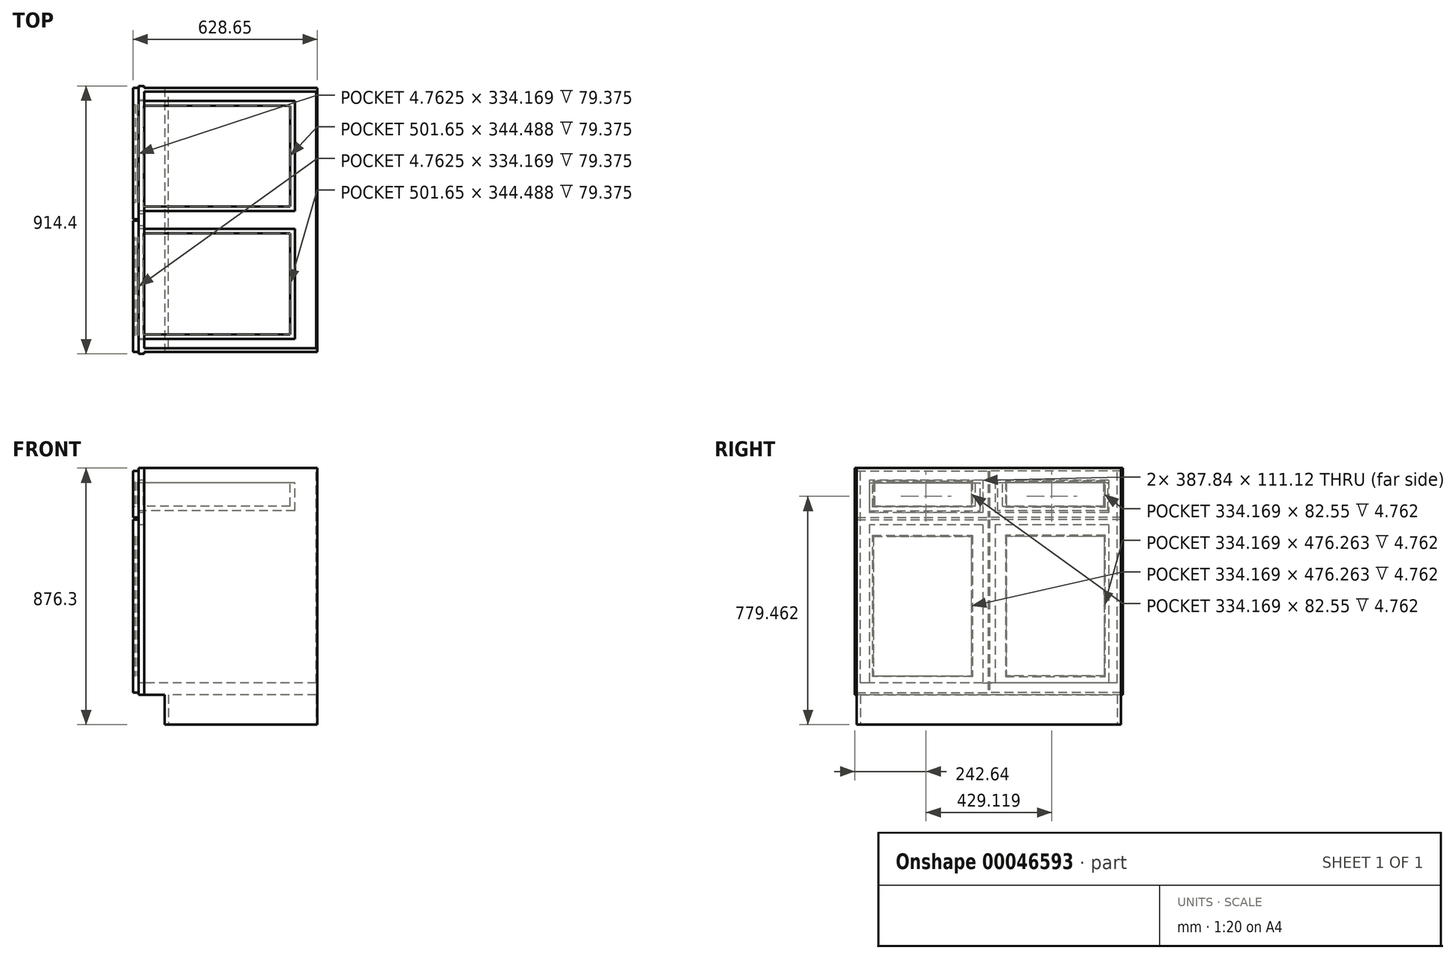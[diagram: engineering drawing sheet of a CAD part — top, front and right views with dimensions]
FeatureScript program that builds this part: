
annotation { "Feature Type Name" : "Feature", "Feature Type Description" : "" }
export const myFeature = defineFeature(function(context is Context, id is Id, definition is map)
    precondition{}
    {
        {
            var Q0;
            Q0=qCreatedBy(makeId("Front.planeOp"),FACE);
            var sketch = newSketch(context, id + "F0", { "sketchPlane" : qUnion([Q0])});
            skLineSegment(sketch, "E0.bottom", {"start": v(-304.8, -438.15) * mm, "end": v(304.8, -438.15) * mm});
            skLineSegment(sketch, "E0.top", {"start": v(-304.8, 438.15) * mm, "end": v(304.8, 438.15) * mm});
            skLineSegment(sketch, "E0.left", {"start": v(-304.8, -438.15) * mm, "end": v(-304.8, 438.15) * mm});
            skLineSegment(sketch, "E0.right", {"start": v(304.8, -438.15) * mm, "end": v(304.8, 438.15) * mm});
            skLineSegment(sketch, "E1", {"start": v(-304.8, -438.15) * mm, "end": v(304.8, 438.15) * mm, "construction": true});
            skSolve(sketch);
        }
        {
            var Q0;
            Q0=qSketchRegion(id+"F0",true);
            extrude(context, id + "F1", {"entities" : qUnion([Q0]), "oppositeDirection" : true, "depth" : 914.4 * mm});
        }
        {
            var Q0;
            Q0=makeQuery(id+"F1.opExtrude","CAP_FACE",FACE,{"disambiguationData":[OSD([sQuery(id+"F0.wireOp",EDGE,"E0.bottom"),sQuery(id+"F0.wireOp",EDGE,"E0.top"),sQuery(id+"F0.wireOp",EDGE,"E0.left"),sQuery(id+"F0.wireOp",EDGE,"E0.right")])],"isStart":true});
            var sketch = newSketch(context, id + "F2", { "sketchPlane" : qUnion([Q0])});
            skLineSegment(sketch, "E2.bottom", {"start": v(-304.8, -438.15) * mm, "end": v(-215.9, -438.15) * mm});
            skLineSegment(sketch, "E2.top", {"start": v(-304.8, -336.55) * mm, "end": v(-215.9, -336.55) * mm});
            skLineSegment(sketch, "E2.left", {"start": v(-304.8, -438.15) * mm, "end": v(-304.8, -336.55) * mm});
            skLineSegment(sketch, "E2.right", {"start": v(-215.9, -438.15) * mm, "end": v(-215.9, -336.55) * mm});
            skSolve(sketch);
        }
        {
            var Q0;
            Q0=qSketchRegion(id+"F2",true);
            extrude(context, id + "F3", {"entities" : qUnion([Q0]), "operationType" : NewBodyOperationType.REMOVE, "endBound" : BoundingType.THROUGH_ALL, "oppositeDirection" : true, "depth" : 25.4 * mm});
        }
        {
            var Q0;
            Q0=makeQuery(id+"F1.opExtrude","SWEPT_FACE",FACE,{"disambiguationData":[OSD([sQuery(id+"F0.wireOp",EDGE,"E0.left")])]});
            var sketch = newSketch(context, id + "F4", { "sketchPlane" : qUnion([Q0])});
            skLineSegment(sketch, "E3.bottom", {"start": v(-865.68, 396.88) * mm, "end": v(-48.72, 396.88) * mm});
            skLineSegment(sketch, "E3.top", {"start": v(-865.68, -295.28) * mm, "end": v(-48.72, -295.28) * mm});
            skLineSegment(sketch, "E3.left", {"start": v(-865.68, 396.88) * mm, "end": v(-865.68, -295.28) * mm});
            skLineSegment(sketch, "E3.right", {"start": v(-48.72, 396.88) * mm, "end": v(-48.72, -295.28) * mm});
            skLineSegment(sketch, "E4", {"start": v(-914.4, 438.15) * mm, "end": v(0, -336.55) * mm, "construction": true});
            skSolve(sketch);
        }
        {
            var Q0;
            Q0=qSketchRegion(id+"F4",true);
            extrude(context, id + "F5", {"entities" : qUnion([Q0]), "operationType" : NewBodyOperationType.REMOVE, "oppositeDirection" : true, "depth" : 19.05 * mm});
        }
        {
            var Q0;
            Q0=makeQuery(id+"F1.opExtrude","SWEPT_FACE",FACE,{"disambiguationData":[OSD([sQuery(id+"F0.wireOp",EDGE,"E0.top")])]});
            var sketch = newSketch(context, id + "F6", { "sketchPlane" : qUnion([Q0])});
            skLineSegment(sketch, "E5.bottom", {"start": v(304.8, 914.4) * mm, "end": v(-285.75, 914.4) * mm});
            skLineSegment(sketch, "E5.top", {"start": v(304.8, 908.05) * mm, "end": v(-285.75, 908.05) * mm});
            skLineSegment(sketch, "E5.left", {"start": v(304.8, 914.4) * mm, "end": v(304.8, 908.05) * mm});
            skLineSegment(sketch, "E5.right", {"start": v(-285.75, 914.4) * mm, "end": v(-285.75, 908.05) * mm});
            skLineSegment(sketch, "E6.bottom", {"start": v(304.8, 0) * mm, "end": v(-285.75, 0) * mm});
            skLineSegment(sketch, "E6.top", {"start": v(304.8, 6.35) * mm, "end": v(-285.75, 6.35) * mm});
            skLineSegment(sketch, "E6.left", {"start": v(304.8, 0) * mm, "end": v(304.8, 6.35) * mm});
            skLineSegment(sketch, "E6.right", {"start": v(-285.75, 0) * mm, "end": v(-285.75, 6.35) * mm});
            skSolve(sketch);
        }
        {
            var Q0;
            Q0=qSketchRegion(id+"F6",true);
            extrude(context, id + "F7", {"entities" : qUnion([Q0]), "operationType" : NewBodyOperationType.REMOVE, "endBound" : BoundingType.THROUGH_ALL, "oppositeDirection" : true, "depth" : 25.4 * mm});
        }
        {
            var Q0;
            Q0=makeQuery(id+"F1.opExtrude","SWEPT_FACE",FACE,{"disambiguationData":[OSD([sQuery(id+"F0.wireOp",EDGE,"E0.top")])]});
            var sketch = newSketch(context, id + "F8", { "sketchPlane" : qUnion([Q0])});
            skLineSegment(sketch, "E7.bottom", {"start": v(301.62, 895.35) * mm, "end": v(-285.75, 895.35) * mm});
            skLineSegment(sketch, "E7.top", {"start": v(301.63, 19.05) * mm, "end": v(-285.75, 19.05) * mm});
            skLineSegment(sketch, "E7.left", {"start": v(301.62, 895.35) * mm, "end": v(301.63, 19.05) * mm});
            skLineSegment(sketch, "E7.right", {"start": v(-285.75, 895.35) * mm, "end": v(-285.75, 19.05) * mm});
            skSolve(sketch);
        }
        {
            var Q0;
            Q0=qSketchRegion(id+"F8",true);
            var Q1;
            Q1=makeQuery(id+"F5.boolean.opBoolean","COPY",FACE,{"derivedFrom":makeQuery(id+"F5.opExtrude","SWEPT_FACE",FACE,{"disambiguationData":[OSD([sQuery(id+"F4.wireOp",EDGE,"E3.top")])]})});
            extrude(context, id + "F9", {"entities" : qUnion([Q0]), "operationType" : NewBodyOperationType.REMOVE, "endBound" : BoundingType.UP_TO_SURFACE, "oppositeDirection" : true, "endBoundEntityFace" : qUnion([Q1]), "depth" : 25.4 * mm});
        }
        {
            var Q0;
            Q0=makeQuery(id+"F1.opExtrude","SWEPT_FACE",FACE,{"disambiguationData":[OSD([sQuery(id+"F0.wireOp",EDGE,"E0.left")])]});
            var sketch = newSketch(context, id + "F10", { "sketchPlane" : qUnion([Q0])});
            skLineSegment(sketch, "E8.bottom", {"start": v(-865.68, 285.75) * mm, "end": v(-48.72, 285.75) * mm});
            skLineSegment(sketch, "E8.top", {"start": v(-865.68, 244.47) * mm, "end": v(-48.72, 244.47) * mm});
            skLineSegment(sketch, "E8.left", {"start": v(-865.68, 285.75) * mm, "end": v(-865.68, 244.47) * mm});
            skLineSegment(sketch, "E8.right", {"start": v(-48.72, 285.75) * mm, "end": v(-48.72, 244.47) * mm});
            skLineSegment(sketch, "E9", {"start": v(-457.2, 396.88) * mm, "end": v(-457.2, -295.28) * mm, "construction": true});
            skLineSegment(sketch, "E10.bottom", {"start": v(-477.84, 396.88) * mm, "end": v(-436.56, 396.88) * mm});
            skLineSegment(sketch, "E10.top", {"start": v(-477.84, -295.28) * mm, "end": v(-436.56, -295.28) * mm});
            skLineSegment(sketch, "E10.left", {"start": v(-477.84, 396.87) * mm, "end": v(-477.84, -295.28) * mm});
            skLineSegment(sketch, "E10.right", {"start": v(-436.56, 396.87) * mm, "end": v(-436.56, -295.28) * mm});
            skSolve(sketch);
        }
        {
            var Q0;
            Q0=qSketchRegion(id+"F10",true);
            var Q1;
            Q1=makeQuery(id+"F9.boolean.opBoolean","COPY",FACE,{"derivedFrom":makeQuery(id+"F9.opExtrude","SWEPT_FACE",FACE,{"disambiguationData":[OSD([sQuery(id+"F8.wireOp",EDGE,"E7.right")])]})});
            extrude(context, id + "F11", {"entities" : qUnion([Q0]), "operationType" : NewBodyOperationType.ADD, "endBound" : BoundingType.UP_TO_SURFACE, "oppositeDirection" : true, "endBoundEntityFace" : qUnion([Q1]), "depth" : 25.4 * mm});
        }
        {
            var Q0;
            Q0=makeQuery(id+"F11.boolean.opBoolean","MERGE",FACE,{"derivedFrom":[makeQuery(id+"F1.opExtrude","SWEPT_FACE",FACE,{"disambiguationData":[OSD([sQuery(id+"F0.wireOp",EDGE,"E0.left")])]}),makeQuery(id+"F11.opExtrude","CAP_FACE",FACE,{"disambiguationData":[OSD([sQuery(id+"F10.wireOp",EDGE,"E8.bottom"),sQuery(id+"F10.wireOp",EDGE,"E8.top"),sQuery(id+"F10.wireOp",EDGE,"E8.left"),sQuery(id+"F10.wireOp",EDGE,"E8.right"),sQuery(id+"F10.wireOp",EDGE,"E10.bottom"),sQuery(id+"F10.wireOp",EDGE,"E10.top"),sQuery(id+"F10.wireOp",EDGE,"E10.left"),sQuery(id+"F10.wireOp",EDGE,"E10.right")])],"isStart":true})]});
            var sketch = newSketch(context, id + "F12", { "sketchPlane" : qUnion([Q0])});
            skLineSegment(sketch, "E11.bottom", {"start": v(-908.05, 261.95) * mm, "end": v(-459.58, 261.95) * mm});
            skLineSegment(sketch, "E11.top", {"start": v(-908.05, -328.61) * mm, "end": v(-459.58, -328.61) * mm});
            skLineSegment(sketch, "E11.left", {"start": v(-908.05, 261.95) * mm, "end": v(-908.05, -328.61) * mm});
            skLineSegment(sketch, "E11.right", {"start": v(-459.58, 261.95) * mm, "end": v(-459.58, -328.61) * mm});
            skLineSegment(sketch, "E12.bottom", {"start": v(-850.9, 204.8) * mm, "end": v(-516.73, 204.8) * mm});
            skLineSegment(sketch, "E12.top", {"start": v(-850.9, -271.46) * mm, "end": v(-516.73, -271.46) * mm});
            skLineSegment(sketch, "E12.left", {"start": v(-850.9, 204.8) * mm, "end": v(-850.9, -271.46) * mm});
            skLineSegment(sketch, "E12.right", {"start": v(-516.73, 204.8) * mm, "end": v(-516.73, -271.46) * mm});
            skSolve(sketch);
        }
        {
            var Q0;
            Q0=qSketchRegion(id+"F12",true);
            extrude(context, id + "F13", {"entities" : qUnion([Q0]), "depth" : 19.05 * mm});
        }
        {
            var Q0;
            Q0=makeQuery(id+"F13.opExtrude","SWEPT_FACE",FACE,{"disambiguationData":[OSD([sQuery(id+"F12.wireOp",EDGE,"E12.top")])]});
            var sketch = newSketch(context, id + "F14", { "sketchPlane" : qUnion([Q0])});
            skLineSegment(sketch, "E13.bottom", {"start": v(-315.91, 850.9) * mm, "end": v(-309.56, 850.9) * mm});
            skLineSegment(sketch, "E13.top", {"start": v(-315.91, 516.73) * mm, "end": v(-309.56, 516.73) * mm});
            skLineSegment(sketch, "E13.left", {"start": v(-315.91, 850.9) * mm, "end": v(-315.91, 516.73) * mm});
            skLineSegment(sketch, "E13.right", {"start": v(-309.56, 850.9) * mm, "end": v(-309.56, 516.73) * mm});
            skSolve(sketch);
        }
        {
            var Q0;
            Q0=qSketchRegion(id+"F14",true);
            extrude(context, id + "F15", {"entities" : qUnion([Q0]), "operationType" : NewBodyOperationType.ADD, "endBound" : BoundingType.UP_TO_NEXT, "depth" : 25.4 * mm});
        }
        {
            var Q0;
            Q0=makeQuery(id+"F13.opExtrude","CAP_EDGE",EDGE,{"disambiguationData":[OSD([sQuery(id+"F12.wireOp",EDGE,"E12.left")])],"isStart":false});
            var Q1;
            Q1=makeQuery(id+"F13.opExtrude","CAP_EDGE",EDGE,{"disambiguationData":[OSD([sQuery(id+"F12.wireOp",EDGE,"E12.top")])],"isStart":false});
            var Q2;
            Q2=makeQuery(id+"F13.opExtrude","CAP_EDGE",EDGE,{"disambiguationData":[OSD([sQuery(id+"F12.wireOp",EDGE,"E12.right")])],"isStart":false});
            var Q3;
            Q3=makeQuery(id+"F13.opExtrude","CAP_EDGE",EDGE,{"disambiguationData":[OSD([sQuery(id+"F12.wireOp",EDGE,"E12.bottom")])],"isStart":false});
            chamfer(context, id + "F16", {"entities" : qUnion([Q0, Q1, Q2, Q3]), "width" : 3.17 * mm, "tangentPropagation" : true});
        }
        {
            var Q0;
            Q0=makeQuery(id+"F11.boolean.opBoolean","MERGE",FACE,{"derivedFrom":[makeQuery(id+"F1.opExtrude","SWEPT_FACE",FACE,{"disambiguationData":[OSD([sQuery(id+"F0.wireOp",EDGE,"E0.left")])]}),makeQuery(id+"F11.opExtrude","CAP_FACE",FACE,{"disambiguationData":[OSD([sQuery(id+"F10.wireOp",EDGE,"E8.bottom"),sQuery(id+"F10.wireOp",EDGE,"E8.top"),sQuery(id+"F10.wireOp",EDGE,"E8.left"),sQuery(id+"F10.wireOp",EDGE,"E8.right"),sQuery(id+"F10.wireOp",EDGE,"E10.bottom"),sQuery(id+"F10.wireOp",EDGE,"E10.top"),sQuery(id+"F10.wireOp",EDGE,"E10.left"),sQuery(id+"F10.wireOp",EDGE,"E10.right")])],"isStart":true})]});
            var sketch = newSketch(context, id + "F17", { "sketchPlane" : qUnion([Q0])});
            skLineSegment(sketch, "E14.bottom", {"start": v(-908.05, 428.62) * mm, "end": v(-459.58, 428.62) * mm});
            skLineSegment(sketch, "E14.top", {"start": v(-908.05, 269.88) * mm, "end": v(-459.58, 269.88) * mm});
            skLineSegment(sketch, "E14.left", {"start": v(-908.05, 428.62) * mm, "end": v(-908.05, 269.88) * mm});
            skLineSegment(sketch, "E14.right", {"start": v(-459.58, 428.62) * mm, "end": v(-459.58, 269.88) * mm});
            skLineSegment(sketch, "E15.bottom", {"start": v(-850.9, 390.52) * mm, "end": v(-516.73, 390.52) * mm});
            skLineSegment(sketch, "E15.top", {"start": v(-850.9, 307.98) * mm, "end": v(-516.73, 307.98) * mm});
            skLineSegment(sketch, "E15.left", {"start": v(-850.9, 390.52) * mm, "end": v(-850.9, 307.98) * mm});
            skLineSegment(sketch, "E15.right", {"start": v(-516.73, 390.52) * mm, "end": v(-516.73, 307.98) * mm});
            skSolve(sketch);
        }
        {
            var Q0;
            Q0=qSketchRegion(id+"F17",true);
            extrude(context, id + "F18", {"entities" : qUnion([Q0]), "depth" : 19.05 * mm});
        }
        {
            var Q0;
            Q0=makeQuery(id+"F18.opExtrude","SWEPT_FACE",FACE,{"disambiguationData":[OSD([sQuery(id+"F17.wireOp",EDGE,"E15.top")])]});
            var sketch = newSketch(context, id + "F19", { "sketchPlane" : qUnion([Q0])});
            skLineSegment(sketch, "E16.bottom", {"start": v(-309.56, 850.9) * mm, "end": v(-315.91, 850.9) * mm});
            skLineSegment(sketch, "E16.top", {"start": v(-309.56, 516.73) * mm, "end": v(-315.91, 516.73) * mm});
            skLineSegment(sketch, "E16.left", {"start": v(-309.56, 850.9) * mm, "end": v(-309.56, 516.73) * mm});
            skLineSegment(sketch, "E16.right", {"start": v(-315.91, 850.9) * mm, "end": v(-315.91, 516.73) * mm});
            skSolve(sketch);
        }
        {
            var Q0;
            Q0=qSketchRegion(id+"F19",true);
            var Q1;
            Q1=makeQuery(id+"F18.opExtrude","SWEPT_FACE",FACE,{"disambiguationData":[OSD([sQuery(id+"F17.wireOp",EDGE,"E15.bottom")])]});
            extrude(context, id + "F20", {"entities" : qUnion([Q0]), "operationType" : NewBodyOperationType.ADD, "endBound" : BoundingType.UP_TO_SURFACE, "endBoundEntityFace" : qUnion([Q1]), "depth" : 25.4 * mm});
        }
        {
            var Q0;
            Q0=makeQuery(id+"F18.opExtrude","CAP_EDGE",EDGE,{"disambiguationData":[OSD([sQuery(id+"F17.wireOp",EDGE,"E15.top")])],"isStart":false});
            var Q1;
            Q1=makeQuery(id+"F18.opExtrude","CAP_EDGE",EDGE,{"disambiguationData":[OSD([sQuery(id+"F17.wireOp",EDGE,"E15.left")])],"isStart":false});
            var Q2;
            Q2=makeQuery(id+"F18.opExtrude","CAP_EDGE",EDGE,{"disambiguationData":[OSD([sQuery(id+"F17.wireOp",EDGE,"E15.bottom")])],"isStart":false});
            var Q3;
            Q3=makeQuery(id+"F18.opExtrude","CAP_EDGE",EDGE,{"disambiguationData":[OSD([sQuery(id+"F17.wireOp",EDGE,"E15.right")])],"isStart":false});
            chamfer(context, id + "F21", {"entities" : qUnion([Q0, Q1, Q2, Q3]), "width" : 3.17 * mm, "tangentPropagation" : true});
        }
        {
            var Q0;
            Q0=makeQuery(id+"F1.opExtrude","SWEPT_FACE",FACE,{"disambiguationData":[OSD([sQuery(id+"F0.wireOp",EDGE,"E0.bottom")])]});
            var sketch = newSketch(context, id + "F22", { "sketchPlane" : qUnion([Q0])});
            skLineSegment(sketch, "E17.bottom", {"start": v(301.63, -19.05) * mm, "end": v(-203.2, -19.05) * mm});
            skLineSegment(sketch, "E17.top", {"start": v(301.63, -895.35) * mm, "end": v(-203.2, -895.35) * mm});
            skLineSegment(sketch, "E17.left", {"start": v(301.63, -19.05) * mm, "end": v(301.63, -895.35) * mm});
            skLineSegment(sketch, "E17.right", {"start": v(-203.2, -19.05) * mm, "end": v(-203.2, -895.35) * mm});
            skSolve(sketch);
        }
        {
            var Q0;
            Q0=qSketchRegion(id+"F22",true);
            extrude(context, id + "F23", {"entities" : qUnion([Q0]), "operationType" : NewBodyOperationType.REMOVE, "oppositeDirection" : true, "depth" : 101.6 * mm});
        }
        {
            var Q0;
            Q0=makeQuery(id+"F18.opExtrude","CAP_FACE",FACE,{"disambiguationData":[OSD([sQuery(id+"F17.wireOp",EDGE,"E14.bottom"),sQuery(id+"F17.wireOp",EDGE,"E14.top"),sQuery(id+"F17.wireOp",EDGE,"E14.left"),sQuery(id+"F17.wireOp",EDGE,"E14.right"),sQuery(id+"F17.wireOp",EDGE,"E15.bottom"),sQuery(id+"F17.wireOp",EDGE,"E15.top"),sQuery(id+"F17.wireOp",EDGE,"E15.left"),sQuery(id+"F17.wireOp",EDGE,"E15.right")])],"isStart":true});
            var sketch = newSketch(context, id + "F24", { "sketchPlane" : qUnion([Q0])});
            skLineSegment(sketch, "E18.bottom", {"start": v(863.6, 292.1) * mm, "end": v(487.36, 292.1) * mm});
            skLineSegment(sketch, "E18.top", {"start": v(863.6, 387.35) * mm, "end": v(487.36, 387.35) * mm});
            skLineSegment(sketch, "E18.left", {"start": v(863.6, 292.1) * mm, "end": v(863.6, 387.35) * mm});
            skLineSegment(sketch, "E18.right", {"start": v(487.36, 292.1) * mm, "end": v(487.36, 387.35) * mm});
            skSolve(sketch);
        }
        {
            var Q0;
            Q0=qSketchRegion(id+"F24",true);
            extrude(context, id + "F25", {"entities" : qUnion([Q0]), "operationType" : NewBodyOperationType.ADD, "depth" : 533.4 * mm});
        }
        {
            var Q0;
            Q0=makeQuery(id+"F25.opExtrude","SWEPT_FACE",FACE,{"disambiguationData":[OSD([sQuery(id+"F24.wireOp",EDGE,"E18.top")])]});
            shell(context, id + "F26", {"entities" : qUnion([Q0]), "thickness" : 15.88 * mm});
        }
        {
            var Q0;
            Q0=sQuery(id+"F10.wireOp",EDGE,"E10.bottom");
            var Q1;
            Q1=sQuery(id+"F10.wireOp",VERTEX,"E9.start");
            cPlane(context, id + "F27", {"entities" : qUnion([Q0, Q1]), "cplaneType" : CPlaneType.LINE_POINT, "offset" : 152.4 * mm, "width" : 152.4 * mm, "height" : 152.4 * mm});
        }
        {
            var Q0;
            Q0=makeQuery(id+"F18.opExtrude","SWEPT_BODY",BODY,{"disambiguationData":[OSD([sQuery(id+"F17.wireOp",EDGE,"E14.bottom"),sQuery(id+"F17.wireOp",EDGE,"E14.top"),sQuery(id+"F17.wireOp",EDGE,"E14.left"),sQuery(id+"F17.wireOp",EDGE,"E14.right"),sQuery(id+"F17.wireOp",EDGE,"E15.bottom"),sQuery(id+"F17.wireOp",EDGE,"E15.top"),sQuery(id+"F17.wireOp",EDGE,"E15.left"),sQuery(id+"F17.wireOp",EDGE,"E15.right")])]});
            var Q1;
            Q1=qCreatedBy(id+"F27.planeOp",FACE);
            mirror(context, id + "F28", {"entities" : qUnion([Q0]), "mirrorPlane" : qUnion([Q1])});
        }
        {
            var Q0;
            Q0=makeQuery(id+"F13.opExtrude","SWEPT_BODY",BODY,{"disambiguationData":[OSD([sQuery(id+"F12.wireOp",EDGE,"E11.bottom"),sQuery(id+"F12.wireOp",EDGE,"E11.top"),sQuery(id+"F12.wireOp",EDGE,"E11.left"),sQuery(id+"F12.wireOp",EDGE,"E11.right"),sQuery(id+"F12.wireOp",EDGE,"E12.bottom"),sQuery(id+"F12.wireOp",EDGE,"E12.top"),sQuery(id+"F12.wireOp",EDGE,"E12.left"),sQuery(id+"F12.wireOp",EDGE,"E12.right")])]});
            var Q1;
            Q1=qCreatedBy(id+"F27.planeOp",FACE);
            mirror(context, id + "F29", {"entities" : qUnion([Q0]), "mirrorPlane" : qUnion([Q1])});
        }
    });
